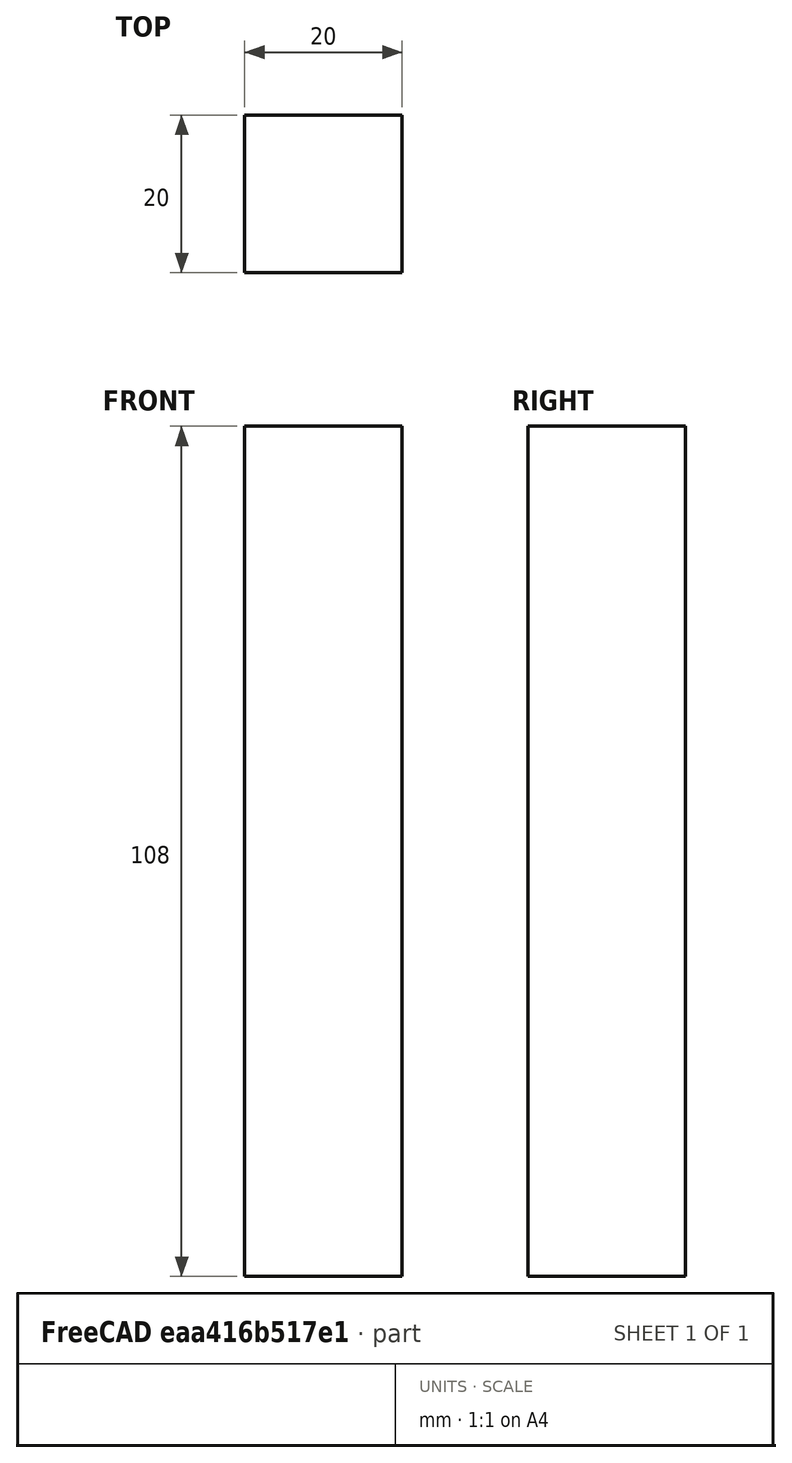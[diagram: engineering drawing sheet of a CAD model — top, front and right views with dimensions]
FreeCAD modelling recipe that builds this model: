
FCSTD DOCUMENT  (FreeCAD 0.19R24276 (Git))
Label: L108
License: All rights reserved
LicenseURL: http://en.wikipedia.org/wiki/All_rights_reserved
objects: Sketcher::SketchObject×1, PartDesign::Pad×1, PartDesign::Body×1
note: 4 computed .brp shape members not serialized (recipe doc carries the construction recipe); baked Part::Feature solids carry a one-line shape summary decoded from their .brp

FEATURE [Sketcher::SketchObject] Sketch
  FullyConstrained = true
  MapMode = 5
  Support = -> [XY_Plane]
  sketch-geometry (4):
    g0: LineSegment StartX=0 StartY=0 StartZ=0 EndX=20 EndY=0 EndZ=0
    g1: LineSegment StartX=20 StartY=0 StartZ=0 EndX=20 EndY=-20 EndZ=0
    g2: LineSegment StartX=20 StartY=-20 StartZ=0 EndX=0 EndY=-20 EndZ=0
    g3: LineSegment StartX=0 StartY=-20 StartZ=0 EndX=0 EndY=0 EndZ=0
  constraints (11):
    c: Coincident(g0,g1)
    c: Coincident(g1,g2)
    c: Coincident(g2,g3)
    c: Coincident(g3,g0)
    c: Horizontal(g0)
    c: Horizontal(g2)
    c: Vertical(g1)
    c: Vertical(g3)
    c: Coincident(g0,g-1)
    c: Equal(g1,g2)
    c: DistanceY(g1,g1) = 20
FEATURE [PartDesign::Pad] Pad
  Direction = (1,1,1)
  Length = 108
  Length2 = 100
  Profile = -> Sketch
  Type = 0
FEATURE [PartDesign::Body] Body
  Group = -> [Sketch,Pad]
  Origin = -> Origin
  Tip = -> Pad
